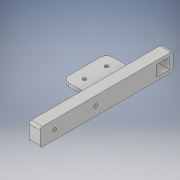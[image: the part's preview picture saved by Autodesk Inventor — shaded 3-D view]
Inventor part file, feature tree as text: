
AUTODESK INVENTOR PART (.ipt)
format: ipt  version: 2018 (Build 220112000, 112)  size: 156,160 bytes
history: native  units: mm
features: extrude x4, sketch x4, fillet x2
ambient origin geometry x8: Origin, YZ Plane, XZ Plane, XY Plane, X Axis, Y Axis, Z Axis, Center Point
bodies: Solid1 (feature_tree)
feature tree (10):
  extrude  "Extrusion1"  Depth=10.0mm
  extrude  "Extrusion2"  Depth=3.0mm
  extrude  "Extrusion4"  Depth=3.0mm
  fillet  "Fillet2"  Radius=10.0mm
  sketch  "Sketch4"  dims[d15=3.2mm d16=55.0mm d17=37.0mm d18=8.0mm d19=8.0mm d20=6.0mm d21=0.0mm d22=3.0mm d23=40.0mm d24=2.0mm d25=30.0mm d32=20.0mm d33=0.0mm d34=6.0mm d35=3.2mm d36=3.2mm d37=10.0mm d38=10.0mm d39=10.0mm d40=10.0mm d41=2.0mm d42=20.0mm d43=0.0mm]
  fillet  "Fillet3"  Radius=3.2mm
  extrude  "Extrusion5"  Depth=55.0mm
  sketch  "Sketch1"  dims[d0=12.0mm d1=10.0mm]
  sketch  "Sketch2"  dims[d4=16.0mm d5=3.0mm]
  sketch  "Sketch3"  dims[d6=120.0mm d7=3.0mm d12=10.0mm d13=0.0mm d14=3.2mm]
